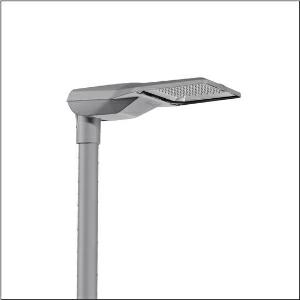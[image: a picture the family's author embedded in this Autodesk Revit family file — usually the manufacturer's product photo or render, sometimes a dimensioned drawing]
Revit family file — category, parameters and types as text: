
# Revit family: streetlight_sl_21_midi___stw1_0a_5xe7e63a08lb_48eb
name_source: partatom
category: Lighting Fixtures
units: mm (PartAtom-declared; Revit-internal decimal feet)

## family parameters
Cut with Voids When Loaded = No
Host = Face
Light Source = No
Part Type = Normal
Room Calculation Point = No
Round Connector Dimension = Use Diameter
Shared = No

## types (1)
- --- (1 x LED, 12860 lm, 98.3 W, 2700K)
    Apparent Load = 98 VA
    CIE Flux Codes = 38 75 98 100 100
    Color Rendering = 70
    Color Temperature = 2700K
    Default Elevation = 1800 mm
    Description = Streetlight SL 21 midi, mast luminaire, primary light control with lens, of PMMA, primary optical cover: cover, of toughened safety glass, transparent, light distribution: STW1.0a, light emission: direct distribution, primary light characteristic: asymmetric, installation type: post-top, side-entry, LED, 3G 1.5mm², High Power LED, rated luminous flux: 12.860lm, luminous efficacy: 131lm/W, light colour: 727, colour temperature: 2700K, control: overheat protection, constant luminous flux control, time-dependent luminous flux control, flexible luminous flux parameterisation, mains connection: 220..240V, AC, 50/60Hz, connection cable pre-assembled, cable length: 10,5m, wiring characteristics: H07RN-F, start of lifetime: 98W, end of service life: 101W, reduction: 44W, luminaire housing, of diecast aluminium, powder-coated, Siteco® metallic grey (DB 702S), corrosivity category C5 mid according to DIN EN ISO 12944, please order mast flange separately, inclination adjustable: 0°, 5°, 10°, 15°, sealing non-destructively replaceable, multi-level sealing system, length: 644mm, width: 335mm, height: 110mm, mast flange for spigot size: 42mm (side-entry): 5XC10008XM4, 60/48mm (side-entry/post-top): 5XC10108XM2, 76/60mm (side-entry/post-top): 5XC10108XM1, protection rating (complete): IP66, insulation class (complete): insulation class II (safety insulation), certification: CE, ENEC, ENEC+, VDE, impact resistance: IK09, permissible operating ambient temperature for outdoor applications: -40..+50°C, standard-compliant lighting for roads and squares, packaging unit: 1 piece

Light Distribution: STW1.0a
    Height = 111 mm
    Lamp = 1 x LED
    Lamp Light Flux = 12860 lm
    Lamp Power = 98.3 W
    Lamp count = 1
    Length = 644 mm
    Luminous efficacy = 131 lm/W
    Manufacturer = Siteco
    ModVariant = No
    Model = 5XE7E63A08LB
    Number of Poles = 1
    OnlyDefault = Yes
    Power Factor = 1
    Product Name = Streetlight SL 21 midi | STW1.0a
    Product group = mast luminaire | pylon top
    ProductGroupID = 6100
    Protection Class = Protection class II
    Protection Degree = IP 66
    RLX_Detail_Level = 1
    RLX_Emergency_Light_Flux = 0 lm
    RLX_Emergency_Type = 0
    RLX_Emergency_Type_DB = No
    RlxData = <blob elided: 91053 chars, md5=700964cf>
    Socket = socket
    Standby Power = 0 W
    System Light Flux = 12860 lm
    System Power = 98 W
    Type Comments = factory setting: luminous flux: 100 % | Output Level: 100 % | 1020 mA
    Type Image = l_1004298.jpg
    URL = http://relux.com
    VarID = @adj_139541
    Voltage = 0 V
    Weight = 0.00 kg
    Width = 336 mm

## geometry (parser evidence)
native form markers: Blend x4, Sweep x12
no freeform markers — native parametric forms only
